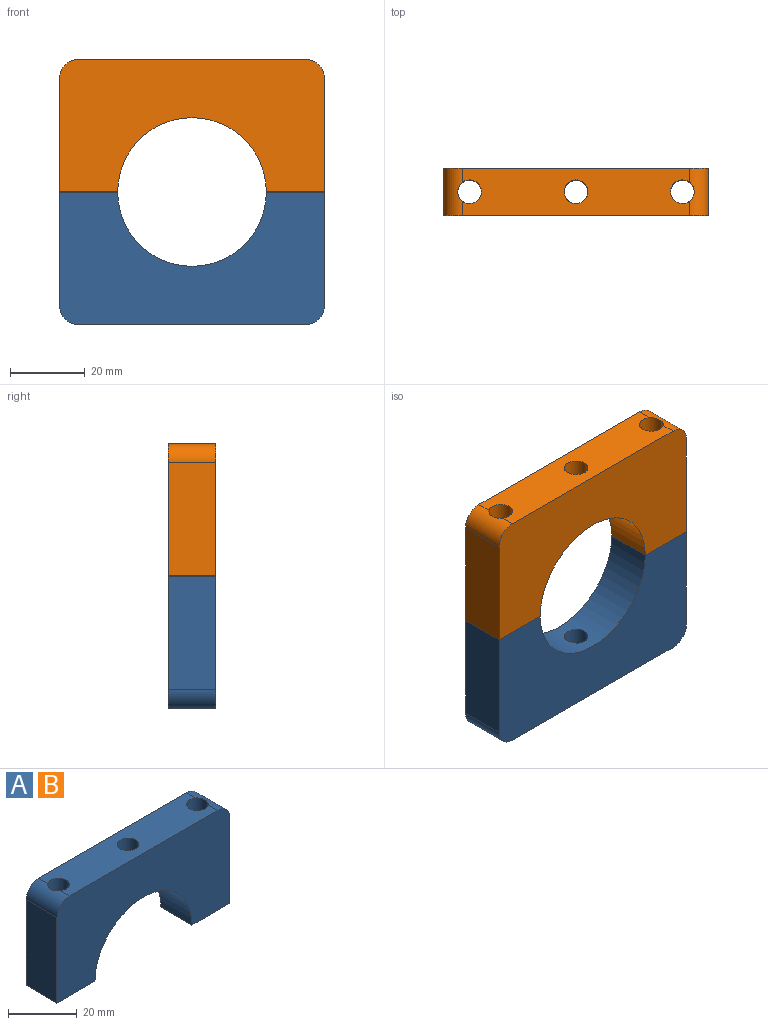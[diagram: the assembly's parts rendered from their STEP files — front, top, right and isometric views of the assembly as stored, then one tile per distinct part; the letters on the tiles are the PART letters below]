
ASSEMBLY  parts=2 mates=1
PART A: 13 faces, bbox 71.1x12.7x35.6 mm
  f0: cylinder r=19.94mm len=39.88mm, axis (0,1,0), area 763.8mm2, adj f1,f5,f6,f7,f10
  f1: plane 15.62x12.7mm, normal (0,0,-1), area 166.7mm2, adj f0,f2,f6,f7,f9
  f2: plane 30.48x12.7mm, normal (1,0,0), area 387.1mm2, adj f1,f6,f7,f11
  f3: plane 60.96x12.7mm, normal (0,0,1), area 688.2mm2, adj f6,f7,f8,f9,f10,f11,f12
  f4: plane 30.48x12.7mm, normal (-1,0,0), area 387.1mm2, adj f5,f6,f7,f12
  f5: plane 15.62x12.7mm, normal (0,0,-1), area 166.7mm2, adj f0,f4,f6,f7,f8
  f6: plane 71.12x35.56mm, normal (0,-1,0), area 1893.5mm2, adj f0,f1,f2,f3,f4,f5,f11,f12
  f7: plane 71.12x35.56mm, normal (0,1,0), area 1893.5mm2, adj f0,f1,f2,f3,f4,f5,f11,f12
  f8: cylinder r=3.17mm len=35.56mm, axis (0,0,1), area 708.9mm2, adj f3,f5,f12
  f9: cylinder r=3.17mm len=35.56mm, axis (0,0,1), area 708.9mm2, adj f1,f3,f11
  f10: cylinder r=3.17mm len=15.88mm, axis (0,0,1), area 314.2mm2, adj f0,f3
  f11: cylinder r=5.08mm len=12.7mm, axis (0,-1,0), area 96.8mm2, adj f2,f3,f6,f7,f9
  f12: cylinder r=5.08mm len=12.7mm, axis (0,1,0), area 96.8mm2, adj f3,f4,f6,f7,f8
PART B: same geometry as A
PLACE A rot(axis=(0,1,0),180deg) t=(56.61,44.79,21.65)mm
PLACE B t=(-14.51,44.79,21.65)mm
MATE parallel A.f8 <-> B.f9  axis (0,0,1) through (49.63,38.44,21.65)mm
